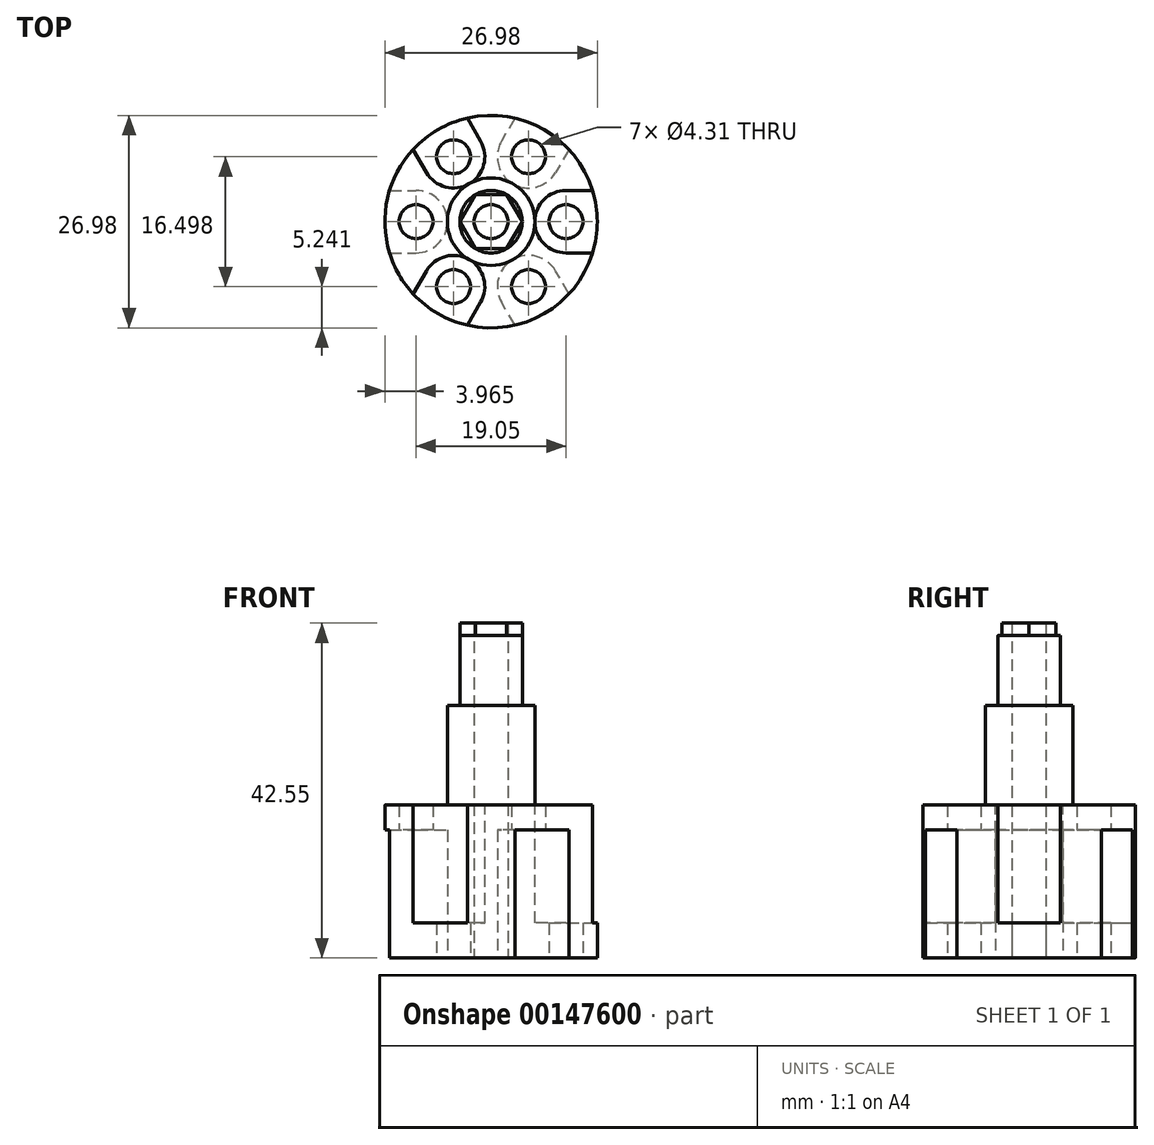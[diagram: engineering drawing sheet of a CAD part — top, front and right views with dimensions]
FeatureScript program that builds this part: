
annotation { "Feature Type Name" : "Feature", "Feature Type Description" : "" }
export const myFeature = defineFeature(function(context is Context, id is Id, definition is map)
    precondition{}
    {
        {
            var Q0;
            Q0=qCreatedBy(makeId("Top.planeOp"),FACE);
            var sketch = newSketch(context, id + "F0", { "sketchPlane" : qUnion([Q0])});
            skCircle(sketch, "E0", {"center": v(0, 0) * mm, "radius": 13.5 * mm});
            skCircle(sketch, "E1", {"center": v(4.76, -8.25) * mm, "radius": 3.97 * mm, "construction": true});
            skCircle(sketch, "E2", {"center": v(0, 0) * mm, "radius": 5.56 * mm, "construction": true});
            skCircle(sketch, "E3.cCircle", {"center": v(0, 0) * mm, "radius": 8.25 * mm, "construction": true});
            skLineSegment(sketch, "E3.0", {"start": v(-4.76, 8.25) * mm, "end": v(4.76, 8.25) * mm, "construction": true});
            skLineSegment(sketch, "E3.1", {"start": v(4.76, 8.25) * mm, "end": v(9.52, 0) * mm, "construction": true});
            skLineSegment(sketch, "E3.2", {"start": v(9.52, 0) * mm, "end": v(4.76, -8.25) * mm, "construction": true});
            skLineSegment(sketch, "E3.3", {"start": v(4.76, -8.25) * mm, "end": v(-4.76, -8.25) * mm, "construction": true});
            skLineSegment(sketch, "E3.4", {"start": v(-4.76, -8.25) * mm, "end": v(-9.52, 0) * mm, "construction": true});
            skLineSegment(sketch, "E3.5", {"start": v(-9.52, 0) * mm, "end": v(-4.76, 8.25) * mm, "construction": true});
            skPoint(sketch, "E3.0.midPoint", {"position": v(0, 8.25) * mm});
            skCircle(sketch, "E4", {"center": v(-4.76, -8.25) * mm, "radius": 2.15 * mm});
            skCircle(sketch, "E5", {"center": v(-9.52, 0) * mm, "radius": 2.15 * mm});
            skCircle(sketch, "E6", {"center": v(-4.76, 8.25) * mm, "radius": 2.15 * mm});
            skCircle(sketch, "E7", {"center": v(4.76, 8.25) * mm, "radius": 2.15 * mm});
            skCircle(sketch, "E8", {"center": v(9.52, 0) * mm, "radius": 2.15 * mm});
            skCircle(sketch, "E9", {"center": v(4.76, -8.25) * mm, "radius": 2.15 * mm});
            skCircle(sketch, "E10", {"center": v(0, 0) * mm, "radius": 2.15 * mm});
            skSolve(sketch);
        }
        {
            var Q0;
            Q0=qSketchRegion(id+"F0",true);
            extrude(context, id + "F1", {"entities" : qUnion([Q0]), "depth" : 19.42 * mm});
        }
        {
            var Q0;
            Q0=makeQuery(id+"F1.opExtrude","CAP_FACE",FACE,{"disambiguationData":[OSD([sQuery(id+"F0.wireOp",EDGE,"E0"),sQuery(id+"F0.wireOp",EDGE,"E4"),sQuery(id+"F0.wireOp",EDGE,"E5"),sQuery(id+"F0.wireOp",EDGE,"E6"),sQuery(id+"F0.wireOp",EDGE,"E7"),sQuery(id+"F0.wireOp",EDGE,"E8"),sQuery(id+"F0.wireOp",EDGE,"E9")])],"isStart":false});
            cPlane(context, id + "F2", {"entities" : qUnion([Q0]), "cplaneType" : CPlaneType.OFFSET, "offset" : 3.17 * mm, "oppositeDirection" : true, "width" : 152.4 * mm, "height" : 152.4 * mm});
        }
        {
            var Q0;
            Q0=makeQuery(id+"F1.opExtrude","CAP_FACE",FACE,{"disambiguationData":[OSD([sQuery(id+"F0.wireOp",EDGE,"E0"),sQuery(id+"F0.wireOp",EDGE,"E4"),sQuery(id+"F0.wireOp",EDGE,"E5"),sQuery(id+"F0.wireOp",EDGE,"E6"),sQuery(id+"F0.wireOp",EDGE,"E7"),sQuery(id+"F0.wireOp",EDGE,"E8"),sQuery(id+"F0.wireOp",EDGE,"E9")])],"isStart":true});
            cPlane(context, id + "F3", {"entities" : qUnion([Q0]), "cplaneType" : CPlaneType.OFFSET, "offset" : 4.44 * mm, "oppositeDirection" : true, "width" : 152.4 * mm, "height" : 152.4 * mm});
        }
        {
            var Q0;
            Q0=makeQuery(id+"F1.opExtrude","CAP_FACE",FACE,{"disambiguationData":[OSD([sQuery(id+"F0.wireOp",EDGE,"E0"),sQuery(id+"F0.wireOp",EDGE,"E4"),sQuery(id+"F0.wireOp",EDGE,"E5"),sQuery(id+"F0.wireOp",EDGE,"E6"),sQuery(id+"F0.wireOp",EDGE,"E7"),sQuery(id+"F0.wireOp",EDGE,"E8"),sQuery(id+"F0.wireOp",EDGE,"E9")])],"isStart":false});
            var sketch = newSketch(context, id + "F4", { "sketchPlane" : qUnion([Q0])});
            skLineSegment(sketch, "E11", {"start": v(-4.76, 8.25) * mm, "end": v(0, 0) * mm, "construction": true});
            skLineSegment(sketch, "E12", {"start": v(9.52, 0) * mm, "end": v(0, 0) * mm, "construction": true});
            skLineSegment(sketch, "E13", {"start": v(0, 0) * mm, "end": v(-4.76, -8.25) * mm, "construction": true});
            skLineSegment(sketch, "E14.bottom", {"start": v(-8.2, 6.26) * mm, "end": v(-1.33, 10.23) * mm, "construction": true});
            skLineSegment(sketch, "E14.top", {"start": v(-10.18, 9.7) * mm, "end": v(-3.3, 13.67) * mm});
            skLineSegment(sketch, "E14.left", {"start": v(-8.2, 6.26) * mm, "end": v(-10.18, 9.7) * mm});
            skLineSegment(sketch, "E14.right", {"start": v(-1.33, 10.23) * mm, "end": v(-3.3, 13.67) * mm});
            skLineSegment(sketch, "E15.bottom", {"start": v(9.52, 3.97) * mm, "end": v(13.5, 3.97) * mm});
            skLineSegment(sketch, "E15.top", {"start": v(9.52, -3.97) * mm, "end": v(13.5, -3.97) * mm});
            skLineSegment(sketch, "E15.left", {"start": v(9.52, 3.97) * mm, "end": v(9.52, -3.97) * mm, "construction": true});
            skLineSegment(sketch, "E15.right", {"start": v(13.5, 3.97) * mm, "end": v(13.5, -3.97) * mm});
            skLineSegment(sketch, "E16.bottom", {"start": v(-8.2, -6.26) * mm, "end": v(-1.33, -10.23) * mm, "construction": true});
            skLineSegment(sketch, "E16.top", {"start": v(-10.18, -9.7) * mm, "end": v(-3.3, -13.67) * mm});
            skLineSegment(sketch, "E16.left", {"start": v(-8.2, -6.26) * mm, "end": v(-10.18, -9.7) * mm});
            skLineSegment(sketch, "E16.right", {"start": v(-1.33, -10.23) * mm, "end": v(-3.3, -13.67) * mm});
            skArc(sketch, "E17", {"start": v(-1.33, -10.23) * mm, "mid": v(-2.78, -4.81) * mm, "end": v(-8.2, -6.26) * mm});
            skArc(sketch, "E18", {"start": v(9.52, 3.97) * mm, "mid": v(5.56, 0) * mm, "end": v(9.52, -3.97) * mm});
            skArc(sketch, "E19", {"start": v(-8.2, 6.26) * mm, "mid": v(-2.78, 4.81) * mm, "end": v(-1.33, 10.23) * mm});
            skSolve(sketch);
        }
        {
            var Q0;
            Q0=qSketchRegion(id+"F4",true);
            var Q1;
            Q1=qCreatedBy(id+"F3.planeOp",FACE);
            extrude(context, id + "F5", {"entities" : qUnion([Q0]), "operationType" : NewBodyOperationType.REMOVE, "endBound" : BoundingType.UP_TO_SURFACE, "oppositeDirection" : true, "endBoundEntityFace" : qUnion([Q1]), "depth" : 25.4 * mm});
        }
        {
            var Q0;
            Q0=makeQuery(id+"F1.opExtrude","CAP_FACE",FACE,{"disambiguationData":[OSD([sQuery(id+"F0.wireOp",EDGE,"E0"),sQuery(id+"F0.wireOp",EDGE,"E4"),sQuery(id+"F0.wireOp",EDGE,"E5"),sQuery(id+"F0.wireOp",EDGE,"E6"),sQuery(id+"F0.wireOp",EDGE,"E7"),sQuery(id+"F0.wireOp",EDGE,"E8"),sQuery(id+"F0.wireOp",EDGE,"E9"),sQuery(id+"F0.wireOp",EDGE,"E10")])],"isStart":true});
            var sketch = newSketch(context, id + "F6", { "sketchPlane" : qUnion([Q0])});
            skLineSegment(sketch, "E20", {"start": v(0, 0) * mm, "end": v(-9.52, 0) * mm, "construction": true});
            skLineSegment(sketch, "E21", {"start": v(0, 0) * mm, "end": v(4.76, 8.25) * mm, "construction": true});
            skLineSegment(sketch, "E22", {"start": v(0, 0) * mm, "end": v(4.76, -8.25) * mm, "construction": true});
            skLineSegment(sketch, "E23.bottom", {"start": v(3.3, -13.67) * mm, "end": v(10.18, -9.7) * mm});
            skLineSegment(sketch, "E23.top", {"start": v(1.33, -10.23) * mm, "end": v(8.2, -6.26) * mm, "construction": true});
            skLineSegment(sketch, "E23.left", {"start": v(3.3, -13.67) * mm, "end": v(1.33, -10.23) * mm});
            skLineSegment(sketch, "E23.right", {"start": v(10.18, -9.7) * mm, "end": v(8.2, -6.26) * mm});
            skLineSegment(sketch, "E24.bottom", {"start": v(3.3, 13.67) * mm, "end": v(10.18, 9.7) * mm});
            skLineSegment(sketch, "E24.top", {"start": v(1.33, 10.23) * mm, "end": v(8.2, 6.26) * mm, "construction": true});
            skLineSegment(sketch, "E24.left", {"start": v(3.3, 13.67) * mm, "end": v(1.33, 10.23) * mm});
            skLineSegment(sketch, "E24.right", {"start": v(10.18, 9.7) * mm, "end": v(8.2, 6.26) * mm});
            skLineSegment(sketch, "E25.bottom", {"start": v(-13.5, 3.97) * mm, "end": v(-9.52, 3.97) * mm});
            skLineSegment(sketch, "E25.top", {"start": v(-13.5, -3.97) * mm, "end": v(-9.52, -3.97) * mm});
            skLineSegment(sketch, "E25.left", {"start": v(-13.5, 3.97) * mm, "end": v(-13.5, -3.97) * mm});
            skLineSegment(sketch, "E25.right", {"start": v(-9.52, 3.97) * mm, "end": v(-9.52, -3.97) * mm, "construction": true});
            skArc(sketch, "E26", {"start": v(8.2, -6.26) * mm, "mid": v(2.78, -4.81) * mm, "end": v(1.33, -10.23) * mm});
            skArc(sketch, "E27", {"start": v(1.33, 10.23) * mm, "mid": v(2.78, 4.81) * mm, "end": v(8.2, 6.26) * mm});
            skArc(sketch, "E28", {"start": v(-9.52, -3.97) * mm, "mid": v(-5.56, 0) * mm, "end": v(-9.52, 3.97) * mm});
            skSolve(sketch);
        }
        {
            var Q0;
            Q0=qSketchRegion(id+"F6",true);
            var Q1;
            Q1=qCreatedBy(id+"F2.planeOp",FACE);
            extrude(context, id + "F7", {"entities" : qUnion([Q0]), "operationType" : NewBodyOperationType.REMOVE, "endBound" : BoundingType.UP_TO_SURFACE, "oppositeDirection" : true, "endBoundEntityFace" : qUnion([Q1]), "depth" : 25.4 * mm});
        }
        {
            var Q0;
            Q0=makeQuery(id+"F1.opExtrude","CAP_FACE",FACE,{"disambiguationData":[OSD([sQuery(id+"F0.wireOp",EDGE,"E0"),sQuery(id+"F0.wireOp",EDGE,"E4"),sQuery(id+"F0.wireOp",EDGE,"E5"),sQuery(id+"F0.wireOp",EDGE,"E6"),sQuery(id+"F0.wireOp",EDGE,"E7"),sQuery(id+"F0.wireOp",EDGE,"E8"),sQuery(id+"F0.wireOp",EDGE,"E9"),sQuery(id+"F0.wireOp",EDGE,"E10")])],"isStart":false});
            var sketch = newSketch(context, id + "F8", { "sketchPlane" : qUnion([Q0])});
            skCircle(sketch, "E29", {"center": v(0, 0) * mm, "radius": 5.56 * mm});
            skCircle(sketch, "E30", {"center": v(0, 0) * mm, "radius": 2.15 * mm});
            skSolve(sketch);
        }
        {
            var Q0;
            Q0=qSketchRegion(id+"F8",true);
            extrude(context, id + "F9", {"entities" : qUnion([Q0]), "operationType" : NewBodyOperationType.ADD, "depth" : 12.65 * mm});
        }
        {
            var Q0;
            Q0=makeQuery(id+"F9.opExtrude","CAP_FACE",FACE,{"disambiguationData":[OSD([sQuery(id+"F8.wireOp",EDGE,"E29"),sQuery(id+"F8.wireOp",EDGE,"E30")])],"isStart":false});
            var sketch = newSketch(context, id + "F10", { "sketchPlane" : qUnion([Q0])});
            skCircle(sketch, "E31", {"center": v(0, 0) * mm, "radius": 3.97 * mm});
            skCircle(sketch, "E32", {"center": v(0, 0) * mm, "radius": 2.15 * mm});
            skSolve(sketch);
        }
        {
            var Q0;
            Q0=qSketchRegion(id+"F10",true);
            extrude(context, id + "F11", {"entities" : qUnion([Q0]), "operationType" : NewBodyOperationType.ADD, "depth" : 8.9 * mm});
        }
        {
            var Q0;
            Q0=makeQuery(id+"F11.opExtrude","CAP_FACE",FACE,{"disambiguationData":[OSD([sQuery(id+"F10.wireOp",EDGE,"E31"),sQuery(id+"F10.wireOp",EDGE,"E32")])],"isStart":false});
            var sketch = newSketch(context, id + "F12", { "sketchPlane" : qUnion([Q0])});
            skCircle(sketch, "E33.cCircle", {"center": v(0, 0) * mm, "radius": 3.97 * mm, "construction": true});
            skLineSegment(sketch, "E33.0", {"start": v(-1.98, 3.44) * mm, "end": v(1.98, 3.44) * mm});
            skLineSegment(sketch, "E33.1", {"start": v(1.98, 3.44) * mm, "end": v(3.97, 0) * mm});
            skLineSegment(sketch, "E33.2", {"start": v(3.97, 0) * mm, "end": v(1.98, -3.44) * mm});
            skLineSegment(sketch, "E33.3", {"start": v(1.98, -3.44) * mm, "end": v(-1.98, -3.44) * mm});
            skLineSegment(sketch, "E33.4", {"start": v(-1.98, -3.44) * mm, "end": v(-3.97, 0) * mm});
            skLineSegment(sketch, "E33.5", {"start": v(-3.97, 0) * mm, "end": v(-1.98, 3.44) * mm});
            skCircle(sketch, "E34", {"center": v(0, 0) * mm, "radius": 2.15 * mm});
            skSolve(sketch);
        }
        {
            var Q0;
            Q0=qSketchRegion(id+"F12",true);
            extrude(context, id + "F13", {"entities" : qUnion([Q0]), "operationType" : NewBodyOperationType.ADD, "depth" : 1.59 * mm});
        }
    });
